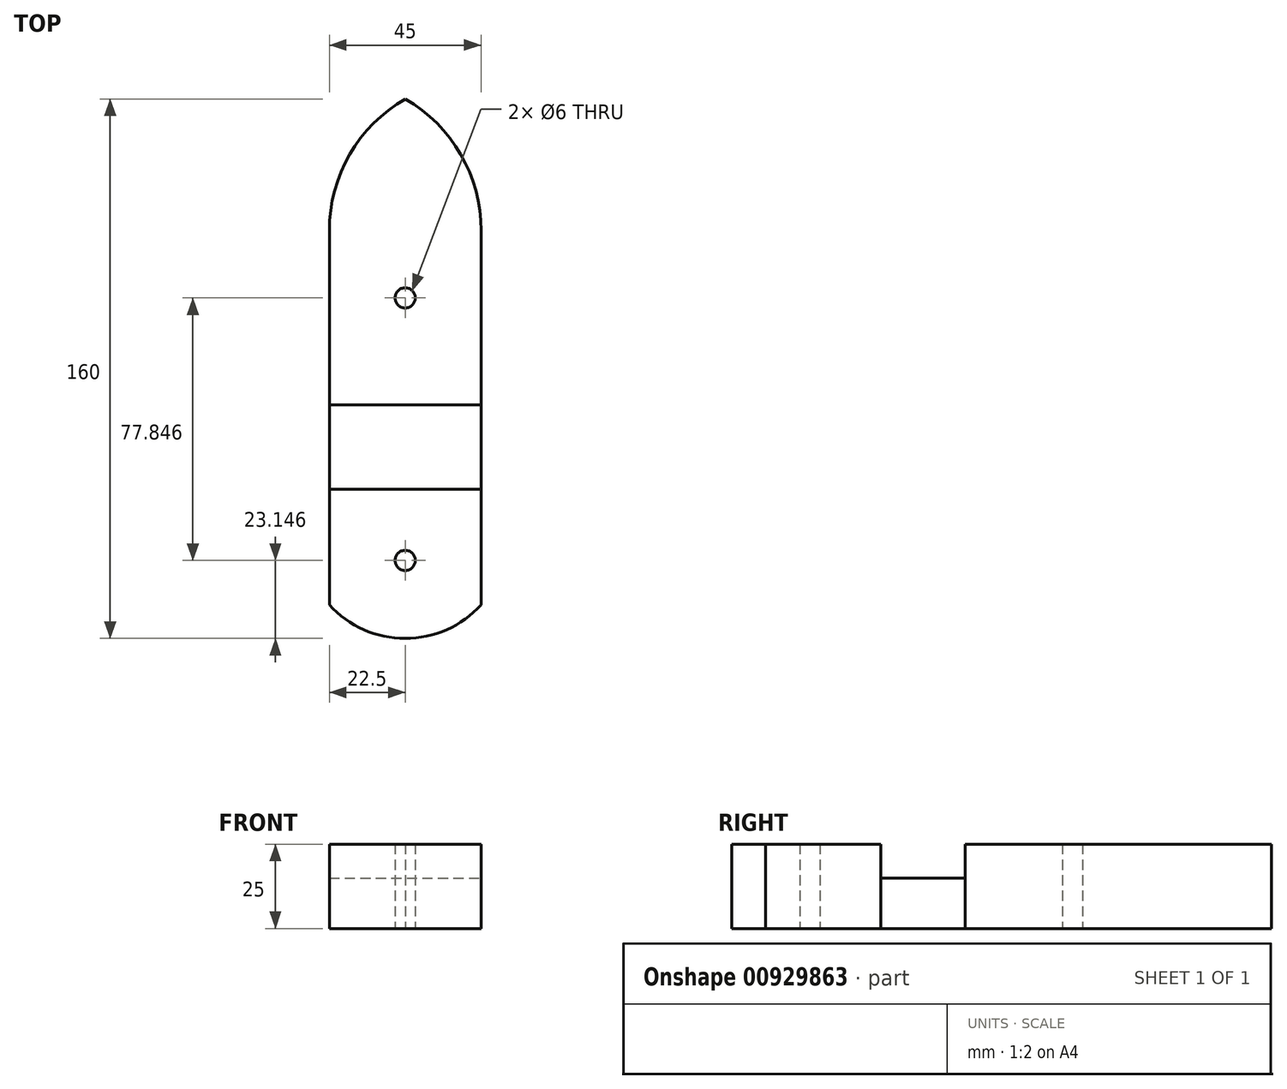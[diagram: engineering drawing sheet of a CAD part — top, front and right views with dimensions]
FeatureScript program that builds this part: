
annotation { "Feature Type Name" : "Feature", "Feature Type Description" : "" }
export const myFeature = defineFeature(function(context is Context, id is Id, definition is map)
    precondition{}
    {
        {
            var Q0;
            Q0=qCreatedBy(makeId("Top.planeOp"),FACE);
            var sketch = newSketch(context, id + "F0", { "sketchPlane" : qUnion([Q0])});
            skLineSegment(sketch, "E0.bottom", {"start": v(-22.5, -55.51) * mm, "end": v(22.5, -55.51) * mm});
            skLineSegment(sketch, "E0.top", {"start": v(-22.5, 55.51) * mm, "end": v(22.5, 55.51) * mm});
            skLineSegment(sketch, "E0.left", {"start": v(-22.5, -55.51) * mm, "end": v(-22.5, 55.51) * mm});
            skLineSegment(sketch, "E0.right", {"start": v(22.5, -55.51) * mm, "end": v(22.5, 55.51) * mm});
            skPoint(sketch, "E0.middle", {"position": v(0, 0) * mm});
            skArc(sketch, "E1", {"start": v(22.5, 55.51) * mm, "mid": v(16.47, 78.01) * mm, "end": v(0, 94.49) * mm});
            skArc(sketch, "E2", {"start": v(-22.5, 55.51) * mm, "mid": v(-16.47, 78.01) * mm, "end": v(0, 94.49) * mm});
            skArc(sketch, "E3", {"start": v(-22.5, -55.51) * mm, "mid": v(0, -65.51) * mm, "end": v(22.5, -55.51) * mm});
            skCircle(sketch, "E4", {"center": v(0, 35.48) * mm, "radius": 3 * mm});
            skCircle(sketch, "E5", {"center": v(0, -42.36) * mm, "radius": 3 * mm});
            skLineSegment(sketch, "E6", {"start": v(-22.5, -21.29) * mm, "end": v(22.5, -21.29) * mm});
            skLineSegment(sketch, "E7", {"start": v(22.5, 3.71) * mm, "end": v(-22.5, 3.71) * mm});
            skPoint(sketch, "E7.endSnap0", {"position": v(-22.5, 0) * mm});
            skSolve(sketch);
        }
        {
            var Q0;
            Q0=makeQuery(id+"F0.imprint","IMPRINT",FACE,{"disambiguationData":[TD([[makeQuery(id+"F0.imprint","IMPRINT",EDGE,{"derivedFrom":sQuery(id+"F0.wireOp",EDGE,"E0.top")}),1.0]])]});
            var Q1;
            {var subQ1=sQuery(id+"F0.wireOp",EDGE,"E0.top");Q1=makeQuery(id+"F0.imprint","IMPRINT",FACE,{"disambiguationData":[TD([[makeQuery(id+"F0.imprint","IMPRINT",EDGE,{"derivedFrom":subQ1}),-1.0]])]});}
            var Q2;
            {var subQ2=sQuery(id+"F0.wireOp",EDGE,"E0.bottom");Q2=makeQuery(id+"F0.imprint","IMPRINT",FACE,{"disambiguationData":[TD([[makeQuery(id+"F0.imprint","IMPRINT",EDGE,{"derivedFrom":subQ2}),1.0]])]});}
            var Q3;
            Q3=makeQuery(id+"F0.imprint","IMPRINT",FACE,{"disambiguationData":[TD([[makeQuery(id+"F0.imprint","IMPRINT",EDGE,{"derivedFrom":sQuery(id+"F0.wireOp",EDGE,"E0.bottom")}),-1.0]])]});
            extrude(context, id + "F1", {"entities" : qUnion([Q0, Q1, Q2, Q3]), "depth" : 25 * mm, "offsetDistance" : 25.4 * mm});
        }
        {
            var Q0;
            {var subQ0=sQuery(id+"F0.wireOp",EDGE,"E6");Q0=makeQuery(id+"F0.imprint","IMPRINT",FACE,{"disambiguationData":[TD([[makeQuery(id+"F0.imprint","IMPRINT",EDGE,{"derivedFrom":subQ0}),1.0]])]});}
            extrude(context, id + "F2", {"entities" : qUnion([Q0]), "depth" : 15 * mm, "offsetDistance" : 25.4 * mm});
        }
    });
